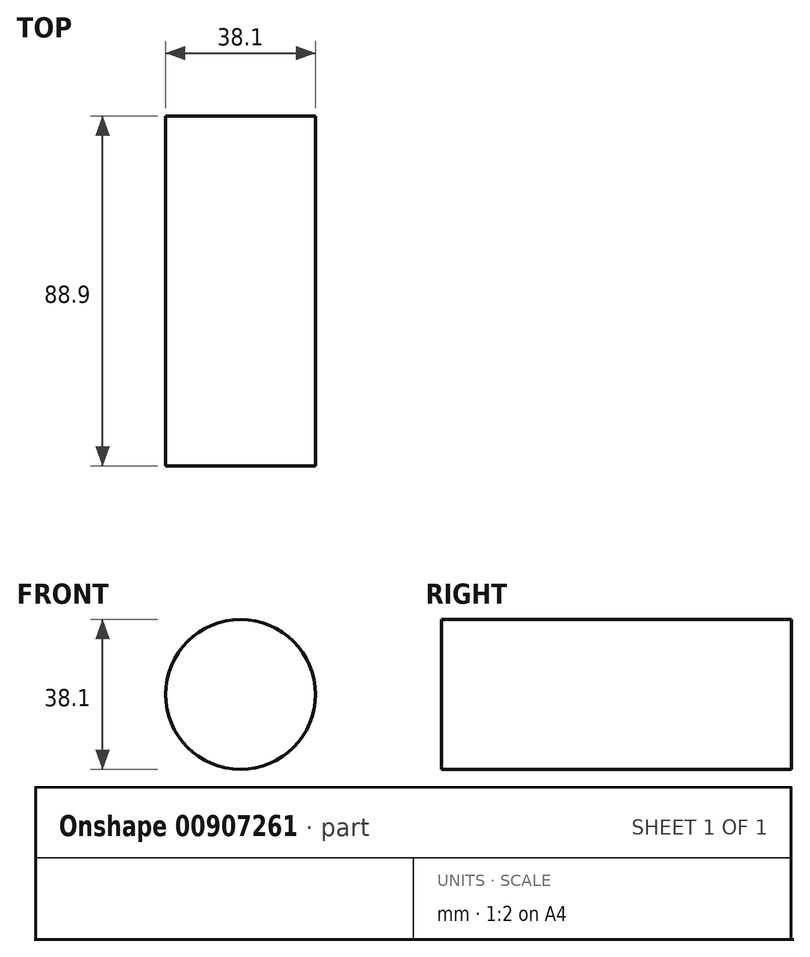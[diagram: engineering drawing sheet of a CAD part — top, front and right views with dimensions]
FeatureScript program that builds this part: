
annotation { "Feature Type Name" : "Feature", "Feature Type Description" : "" }
export const myFeature = defineFeature(function(context is Context, id is Id, definition is map)
    precondition{}
    {
        {
            var Q0;
            Q0=qCreatedBy(makeId("Front.planeOp"),FACE);
            var sketch = newSketch(context, id + "F0", { "sketchPlane" : qUnion([Q0])});
            skCircle(sketch, "E0", {"center": v(0, 0) * mm, "radius": 19.05 * mm});
            skSolve(sketch);
        }
        {
            var Q0;
            Q0 = qSketchRegion(id + "F0", true);
            extrude(context, id + "F1", {"entities" : qUnion([Q0]), "depth" : 88.9 * mm, "offsetDistance" : 25.4 * mm});
        }
    });
